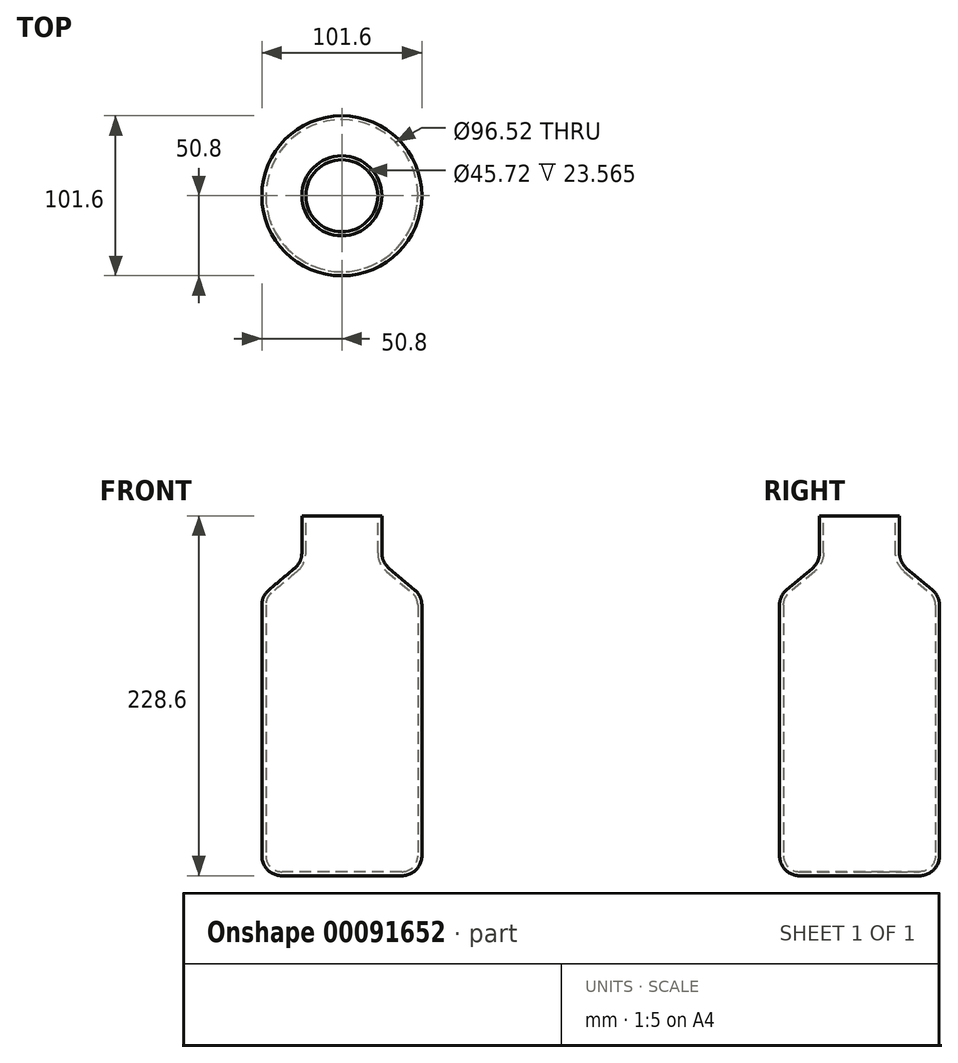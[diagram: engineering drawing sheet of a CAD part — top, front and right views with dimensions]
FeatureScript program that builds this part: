
annotation { "Feature Type Name" : "Feature", "Feature Type Description" : "" }
export const myFeature = defineFeature(function(context is Context, id is Id, definition is map)
    precondition{}
    {
        {
            var Q0;
            Q0=qCreatedBy(makeId("Top.planeOp"),FACE);
            var sketch = newSketch(context, id + "F0", { "sketchPlane" : qUnion([Q0])});
            skCircle(sketch, "E0", {"center": v(0, 0) * mm, "radius": 50.8 * mm});
            skSolve(sketch);
        }
        {
            var Q0;
            Q0=makeQuery(id+"F0.imprint","IMPRINT",FACE,{"disambiguationData":[TD([[makeQuery(id+"F0.imprint","IMPRINT",EDGE,{"derivedFrom":sQuery(id+"F0.wireOp",EDGE,"E0")}),1.0]])]});
            extrude(context, id + "F1", {"entities" : qUnion([Q0]), "depth" : 177.8 * mm});
        }
        {
            var Q0;
            Q0=qCreatedBy(makeId("Front.planeOp"),FACE);
            var sketch = newSketch(context, id + "F2", { "sketchPlane" : qUnion([Q0])});
            skLineSegment(sketch, "E1", {"start": v(0, 177.8) * mm, "end": v(-50.8, 177.8) * mm});
            skLineSegment(sketch, "E2", {"start": v(-50.8, 177.8) * mm, "end": v(-25.4, 199.11) * mm});
            skLineSegment(sketch, "E3", {"start": v(-25.4, 199.11) * mm, "end": v(-25.4, 228.6) * mm});
            skLineSegment(sketch, "E4", {"start": v(-25.4, 228.6) * mm, "end": v(0, 228.6) * mm});
            skLineSegment(sketch, "E5", {"start": v(0, 228.6) * mm, "end": v(0, 177.8) * mm});
            skSolve(sketch);
        }
        {
            var Q0;
            Q0 = qSketchRegion(id + "F2", true);
            var Q1;
            Q1=sQuery(id+"F2.wireOp",EDGE,"E5");
            revolve(context, id + "F3", {"operationType" : NewBodyOperationType.ADD, "entities" : qUnion([Q0]), "axis" : qUnion([Q1]), "revolveType" : RevolveType.FULL});
        }
        {
            var Q0;
            Q0=makeQuery(id+"F1.opExtrude","CAP_EDGE",EDGE,{"disambiguationData":[OSD([sQuery(id+"F0.wireOp",EDGE,"E0")])],"isStart":true});
            var Q1;
            Q1=makeQuery(id+"F3.boolean.opBoolean","MERGE",EDGE,{"derivedFrom":[makeQuery(id+"F1.opExtrude","CAP_EDGE",EDGE,{"disambiguationData":[OSD([sQuery(id+"F0.wireOp",EDGE,"E0")])],"isStart":false}),makeQuery(id+"F3.opRevolve","SWEPT_EDGE",EDGE,{"disambiguationData":[OSD([sQuery(id+"F2.wireOp",EDGE,"E1"),sQuery(id+"F2.wireOp",EDGE,"E2")])]})]});
            var Q2;
            Q2=makeQuery(id+"F3.opRevolve","SWEPT_EDGE",EDGE,{"disambiguationData":[OSD([sQuery(id+"F2.wireOp",EDGE,"E2"),sQuery(id+"F2.wireOp",EDGE,"E3")])]});
            fillet(context, id + "F4", {"entities" : qUnion([Q0, Q1, Q2]), "radius" : 12.7 * mm, "tangentPropagation" : true, "allowEdgeOverflow" : false});
        }
        {
            var Q0;
            Q0=makeQuery(id+"F3.opRevolve","SWEPT_FACE",FACE,{"disambiguationData":[OSD([sQuery(id+"F2.wireOp",EDGE,"E4")])]});
            shell(context, id + "F5", {"entities" : qUnion([Q0]), "thickness" : 2.54 * mm});
        }
    });
